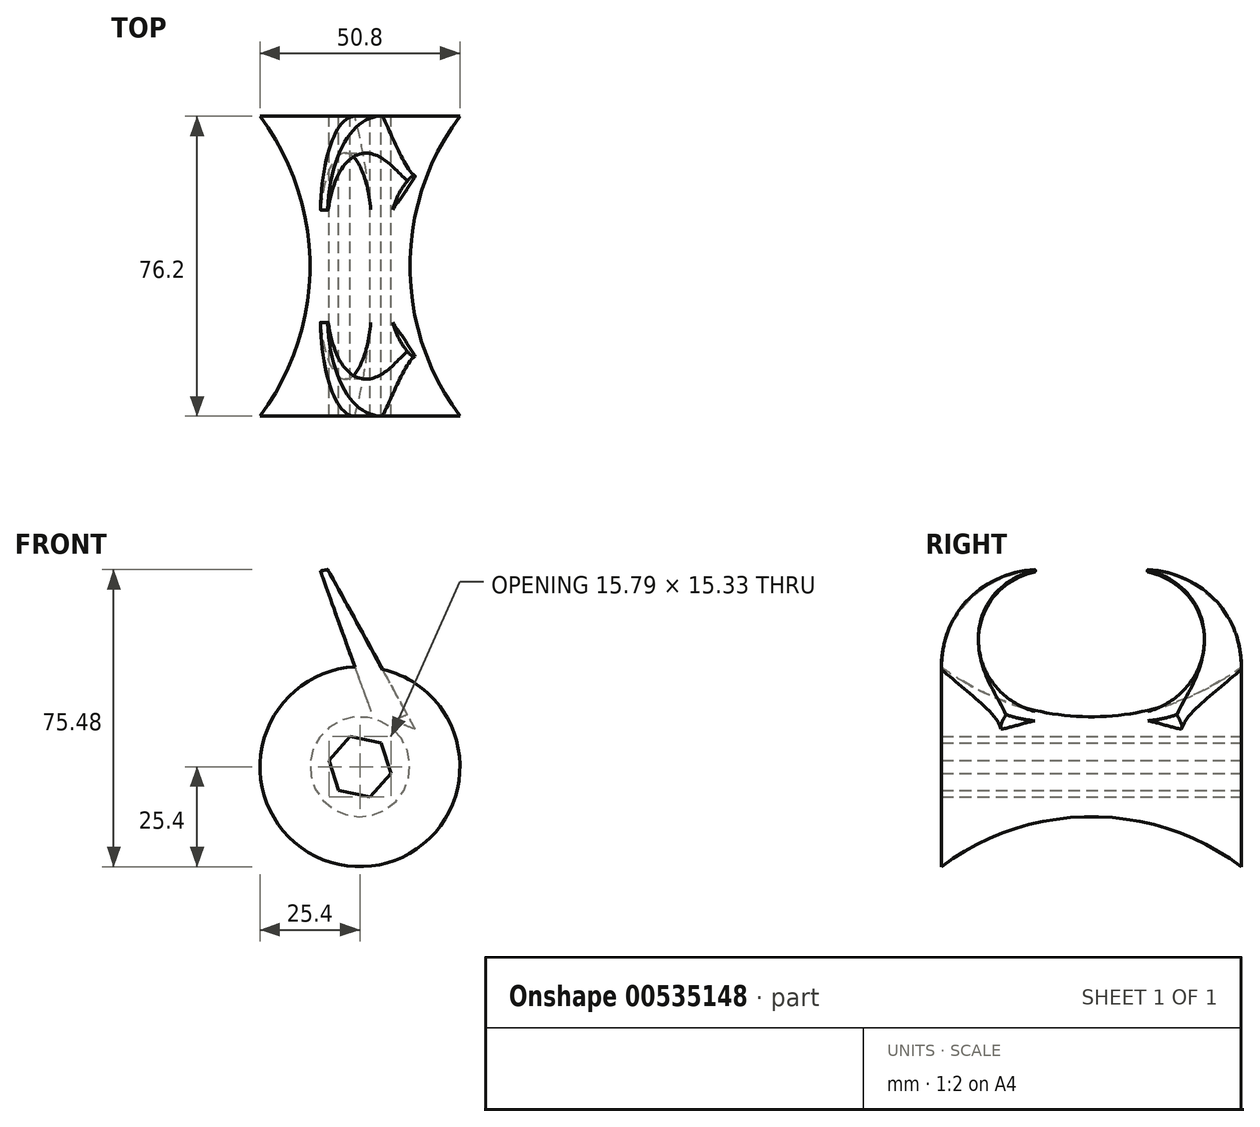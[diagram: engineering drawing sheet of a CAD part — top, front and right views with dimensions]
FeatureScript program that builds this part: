
annotation { "Feature Type Name" : "Feature", "Feature Type Description" : "" }
export const myFeature = defineFeature(function(context is Context, id is Id, definition is map)
    precondition{}
    {
        {
            var Q0;
            Q0=qCreatedBy(makeId("Top.planeOp"),FACE);
            var sketch = newSketch(context, id + "F0", { "sketchPlane" : qUnion([Q0])});
            skLineSegment(sketch, "E0", {"start": v(0, 0) * mm, "end": v(0, 76.2) * mm});
            skLineSegment(sketch, "E1", {"start": v(0, 0) * mm, "end": v(-25.4, 0) * mm});
            skLineSegment(sketch, "E2", {"start": v(0, 76.2) * mm, "end": v(-25.4, 76.2) * mm});
            skArc(sketch, "E3", {"start": v(-25.4, 0) * mm, "mid": v(-12.7, 38.1) * mm, "end": v(-25.4, 76.2) * mm});
            skLineSegment(sketch, "E4", {"start": v(0, 38.1) * mm, "end": v(-6.35, 38.1) * mm, "construction": true});
            skPoint(sketch, "E4.endSnap0", {"position": v(-12.7, 38.1) * mm});
            skSolve(sketch);
        }
        {
            var Q0;
            Q0=makeQuery(id+"F0.imprint","IMPRINT",FACE,{"disambiguationData":[TD([[makeQuery(id+"F0.imprint","IMPRINT",EDGE,{"derivedFrom":sQuery(id+"F0.wireOp",EDGE,"E0")}),1.0]])]});
            var Q1;
            Q1=sQuery(id+"F0.wireOp",EDGE,"E0");
            revolve(context, id + "F1", {"entities" : qUnion([Q0]), "axis" : qUnion([Q1]), "revolveType" : RevolveType.FULL});
        }
        {
            var Q0;
            Q0=makeQuery(id+"F1.opRevolve","SWEPT_FACE",FACE,{"disambiguationData":[OSD([sQuery(id+"F0.wireOp",EDGE,"E2")])]});
            var sketch = newSketch(context, id + "F2", { "sketchPlane" : qUnion([Q0])});
            skCircle(sketch, "E5.cCircle", {"center": v(0, 0) * mm, "radius": 6.99 * mm, "construction": true});
            skLineSegment(sketch, "E5.0", {"start": v(-2.51, -7.66) * mm, "end": v(-7.9, -1.66) * mm});
            skLineSegment(sketch, "E5.1", {"start": v(-7.9, -1.66) * mm, "end": v(-5.38, 6) * mm});
            skLineSegment(sketch, "E5.2", {"start": v(-5.38, 6) * mm, "end": v(2.51, 7.66) * mm});
            skLineSegment(sketch, "E5.3", {"start": v(2.51, 7.66) * mm, "end": v(7.9, 1.66) * mm});
            skLineSegment(sketch, "E5.4", {"start": v(7.9, 1.66) * mm, "end": v(5.38, -6) * mm});
            skLineSegment(sketch, "E5.5", {"start": v(5.38, -6) * mm, "end": v(-2.51, -7.66) * mm});
            skPoint(sketch, "E5.0.midPoint", {"position": v(-5.2, -4.66) * mm});
            skSolve(sketch);
        }
        {
            var Q0;
            Q0=qSketchRegion(id+"F2",true);
            extrude(context, id + "F3", {"entities" : qUnion([Q0]), "operationType" : NewBodyOperationType.REMOVE, "endBound" : BoundingType.THROUGH_ALL, "oppositeDirection" : true, "depth" : 25.4 * mm});
        }
        {
            var Q0;
            Q0=qCreatedBy(makeId("Right.planeOp"),FACE);
            var sketch = newSketch(context, id + "F4", { "sketchPlane" : qUnion([Q0])});
            skLineSegment(sketch, "E6.top", {"start": v(0, 12.7) * mm, "end": v(76.2, 12.7) * mm});
            skLineSegment(sketch, "E7", {"start": v(38.1, 12.7) * mm, "end": v(38.1, 32.91) * mm});
            skLineSegment(sketch, "E8", {"start": v(23.52, 66.48) * mm, "end": v(0, 66.48) * mm});
            skArc(sketch, "E9", {"start": v(23.75, 14.34) * mm, "mid": v(38.1, 12.7) * mm, "end": v(52.45, 14.34) * mm});
            skLineSegment(sketch, "E10", {"start": v(0, 66.48) * mm, "end": v(0, 25.4) * mm});
            skArc(sketch, "E11", {"start": v(0, 25.4) * mm, "mid": v(38.1, 12.7) * mm, "end": v(76.2, 25.4) * mm});
            skPoint(sketch, "E12", {"position": v(76.2, 25.4) * mm});
            skLineSegment(sketch, "E13", {"start": v(48.9, 66.48) * mm, "end": v(76.2, 66.48) * mm});
            skLineSegment(sketch, "E14", {"start": v(76.2, 66.48) * mm, "end": v(76.2, 25.4) * mm});
            skLineSegment(sketch, "E15.bottom", {"start": v(23.52, 66.48) * mm, "end": v(48.9, 66.48) * mm});
            skArc(sketch, "E16", {"start": v(25.4, 50.8) * mm, "mid": v(9.4, 33.26) * mm, "end": v(23.75, 14.34) * mm});
            skArc(sketch, "E17", {"start": v(25.4, 50.8) * mm, "mid": v(7.44, 43.36) * mm, "end": v(0, 25.4) * mm});
            skArc(sketch, "E18.MirrorCS", {"start": v(50.8, 50.8) * mm, "mid": v(66.8, 33.26) * mm, "end": v(52.45, 14.34) * mm});
            skArc(sketch, "E19.MirrorCS", {"start": v(50.8, 50.8) * mm, "mid": v(68.76, 43.36) * mm, "end": v(76.2, 25.4) * mm});
            skSolve(sketch);
        }
        {
            var Q0;
            Q0=qCreatedBy(makeId("Front.planeOp"),FACE);
            var sketch = newSketch(context, id + "F5", { "sketchPlane" : qUnion([Q0])});
            skLineSegment(sketch, "E20", {"start": v(4.23, 9.95) * mm, "end": v(-13.99, 60.71) * mm});
            skLineSegment(sketch, "E21", {"start": v(-13.99, 60.71) * mm, "end": v(12.04, 13.2) * mm});
            skLineSegment(sketch, "E22", {"start": v(12.04, 13.2) * mm, "end": v(4.23, 9.95) * mm});
            skSolve(sketch);
        }
        {
            var Q0;
            Q0=qSketchRegion(id+"F5",true);
            var Q1;
            Q1=makeQuery(id+"F1.opRevolve","SWEPT_FACE",FACE,{"disambiguationData":[OSD([sQuery(id+"F0.wireOp",EDGE,"E2")])]});
            extrude(context, id + "F6", {"entities" : qUnion([Q0]), "operationType" : NewBodyOperationType.ADD, "endBound" : BoundingType.UP_TO_SURFACE, "oppositeDirection" : true, "endBoundEntityFace" : qUnion([Q1]), "depth" : 25.4 * mm});
        }
        {
            var Q0;
            Q0=makeQuery(id+"F4.imprint","IMPRINT",FACE,{"disambiguationData":[TD([[makeQuery(id+"F4.imprint","IMPRINT",EDGE,{"derivedFrom":sQuery(id+"F4.wireOp",EDGE,"E8")}),1.0]])]});
            var Q1;
            Q1=sQuery(id+"F0.wireOp",EDGE,"E0");
            revolve(context, id + "F7", {"operationType" : NewBodyOperationType.REMOVE, "entities" : qUnion([Q0]), "axis" : qUnion([Q1]), "revolveType" : RevolveType.FULL, "oppositeDirection" : true});
        }
        {
            var Q0;
            {var subQ0=makeQuery(id+"F1.opRevolve","SWEPT_FACE",FACE,{"disambiguationData":[OSD([sQuery(id+"F0.wireOp",EDGE,"E3")])]});var subQ1=makeQuery(id+"F6.opExtrude","SWEPT_FACE",FACE,{"disambiguationData":[OSD([sQuery(id+"F5.wireOp",EDGE,"E22")])]});Q0=makeQuery(id+"F7.boolean.opBoolean","SPLIT",EDGE,{"disambiguationData":[TD([makeQuery(id+"F7.opRevolve","SWEPT_FACE",FACE,{"disambiguationData":[OSD([sQuery(id+"F4.wireOp",EDGE,"E16")])]})])],"derivedFrom":makeQuery(id+"F6.boolean.opBoolean","INTERSECT",EDGE,{"derivedFrom":[subQ0,subQ1]})});}
            var Q1;
            {var subQ0=makeQuery(id+"F1.opRevolve","SWEPT_FACE",FACE,{"disambiguationData":[OSD([sQuery(id+"F0.wireOp",EDGE,"E3")])]});var subQ1=makeQuery(id+"F6.opExtrude","SWEPT_FACE",FACE,{"disambiguationData":[OSD([sQuery(id+"F5.wireOp",EDGE,"E22")])]});Q1=makeQuery(id+"F7.boolean.opBoolean","SPLIT",EDGE,{"disambiguationData":[TD([makeQuery(id+"F7.opRevolve","SWEPT_FACE",FACE,{"disambiguationData":[OSD([sQuery(id+"F4.wireOp",EDGE,"E18.MirrorCS")])]})])],"derivedFrom":makeQuery(id+"F6.boolean.opBoolean","INTERSECT",EDGE,{"derivedFrom":[subQ0,subQ1]})});}
            fillet(context, id + "F8", {"entities" : qUnion([Q0, Q1]), "radius" : 5.08 * mm, "tangentPropagation" : true, "allowEdgeOverflow" : false});
        }
        {
            var Q0;
            Q0=makeQuery(id+"F7.boolean.opBoolean","COPY",EDGE,{"derivedFrom":makeQuery(id+"F7.opRevolve","SWEPT_EDGE",EDGE,{"disambiguationData":[OSD([sQuery(id+"F4.wireOp",EDGE,"E18.MirrorCS"),sQuery(id+"F4.wireOp",EDGE,"E19.MirrorCS")])]})});
            var Q1;
            Q1=makeQuery(id+"F7.boolean.opBoolean","COPY",EDGE,{"derivedFrom":makeQuery(id+"F7.opRevolve","SWEPT_EDGE",EDGE,{"disambiguationData":[OSD([sQuery(id+"F4.wireOp",EDGE,"E16"),sQuery(id+"F4.wireOp",EDGE,"E17")])]})});
            fillet(context, id + "F9", {"entities" : qUnion([Q0, Q1]), "radius" : 0.13 * mm, "tangentPropagation" : true, "allowEdgeOverflow" : false});
        }
    });
